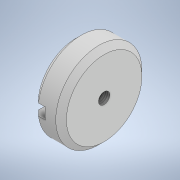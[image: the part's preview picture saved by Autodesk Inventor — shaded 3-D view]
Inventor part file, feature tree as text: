
AUTODESK INVENTOR PART (.ipt)
format: ipt  version: 2022 (Build 260153000, 153)  size: 144,384 bytes
history: native  units: mm
features: sketch x3, revolve x2, other x1, extrude x1, thread x1
ambient origin geometry x8: Origin, YZ Plane, XZ Plane, XY Plane, X Axis, Y Axis, Z Axis, Center Point
bodies: Body1 (feature_tree)
feature tree (8):
  other  "Твердое тело1"
  revolve  "Вращение1"
  revolve  "Вращение2"
  extrude  "Выдавливание1"  Depth=20.0mm
  thread  "Резьба1"
  sketch  "Эскиз1"
  sketch  "Эскиз2"
  sketch  "Эскиз3"
